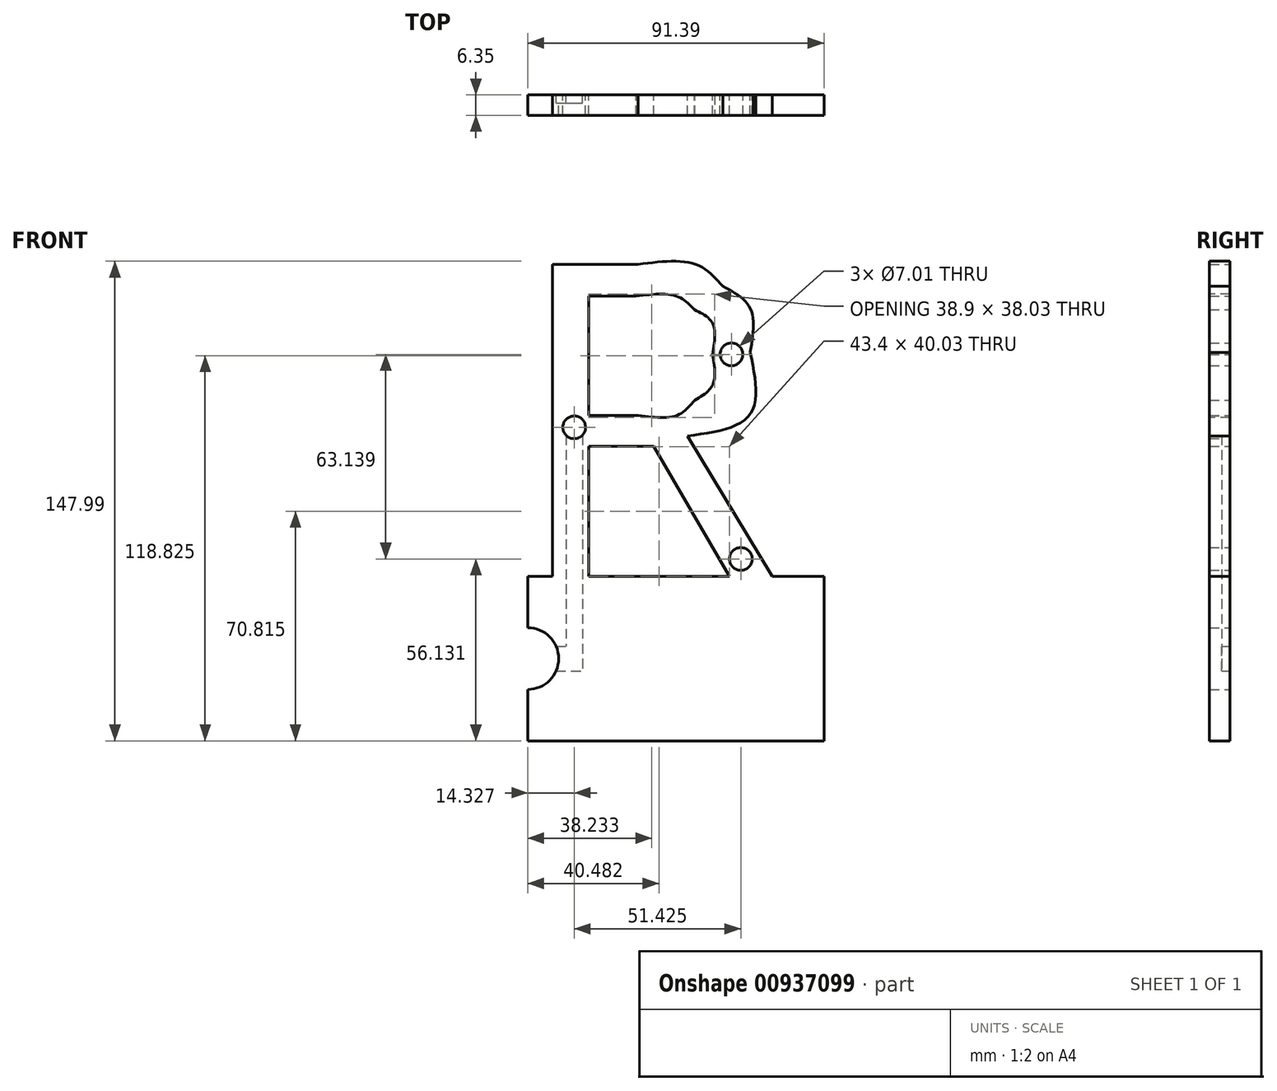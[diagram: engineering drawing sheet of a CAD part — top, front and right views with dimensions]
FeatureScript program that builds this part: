
annotation { "Feature Type Name" : "Feature", "Feature Type Description" : "" }
export const myFeature = defineFeature(function(context is Context, id is Id, definition is map)
    precondition{}
    {
        {
            var Q0;
            Q0=qCreatedBy(makeId("Front.planeOp"),FACE);
            var sketch = newSketch(context, id + "F0", { "sketchPlane" : qUnion([Q0])});
            skText(sketch, "E0", { "text": "R", "fontName": "OpenSans-Regular.ttf"});
            const initialGuessF0  = {"E0": [-0.0449, -0.04854, 1, 0, 0.09708]};
            skSetInitialGuess(sketch, initialGuessF0);
            skSolve(sketch);
        }
        {
            var Q0;
            Q0=qCreatedBy(makeId("Front.planeOp"),FACE);
            var sketch = newSketch(context, id + "F1", { "sketchPlane" : qUnion([Q0])});
            skLineSegment(sketch, "E1.0.0", {"start": v(-5.92, 37.9) * mm, "end": v(-20.48, 37.9) * mm});
            skLineSegment(sketch, "E1.0.1", {"start": v(-20.48, 37.9) * mm, "end": v(-20.48, 1.1) * mm});
            skLineSegment(sketch, "E1.0.2", {"start": v(-20.48, 1.1) * mm, "end": v(-5.12, 1.1) * mm});
            skFitSpline(sketch, "E1.0.3", {"points": [v(-5.12, 1.1) * mm, v(6.72, 1.1) * mm, v(12.25, 5.8) * mm]});
            skFitSpline(sketch, "E1.0.4", {"points": [v(12.25, 5.8) * mm, v(17.78, 10.51) * mm, v(17.78, 19.93) * mm]});
            skFitSpline(sketch, "E1.0.5", {"points": [v(17.78, 19.93) * mm, v(17.78, 29.47) * mm, v(12.16, 33.69) * mm]});
            skFitSpline(sketch, "E1.0.6", {"points": [v(12.16, 33.69) * mm, v(6.53, 37.9) * mm, v(-5.92, 37.9) * mm]});
            skLineSegment(sketch, "E2.0.0", {"start": v(-20.48, -8.51) * mm, "end": v(-0.38, -8.51) * mm});
            skLineSegment(sketch, "E2.0.1", {"start": v(-0.38, -8.51) * mm, "end": v(22.92, -48.54) * mm});
            skLineSegment(sketch, "E2.0.2", {"start": v(22.92, -48.54) * mm, "end": v(36.15, -48.54) * mm});
            skLineSegment(sketch, "E2.0.3", {"start": v(36.15, -48.54) * mm, "end": v(10, -5.29) * mm});
            skFitSpline(sketch, "E2.0.4", {"points": [v(10, -5.29) * mm, v(29.37, 1.43) * mm, v(29.37, 20.52) * mm]});
            skFitSpline(sketch, "E2.0.5", {"points": [v(29.37, 20.52) * mm, v(29.37, 34.15) * mm, v(20.9, 40.93) * mm]});
            skFitSpline(sketch, "E2.0.6", {"points": [v(20.9, 40.93) * mm, v(12.45, 47.72) * mm, v(-5.27, 47.72) * mm]});
            skLineSegment(sketch, "E2.0.7", {"start": v(-5.27, 47.72) * mm, "end": v(-31.66, 47.72) * mm});
            skLineSegment(sketch, "E2.0.8", {"start": v(-31.66, 47.72) * mm, "end": v(-31.66, -48.54) * mm});
            skLineSegment(sketch, "E2.0.9", {"start": v(-31.66, -48.54) * mm, "end": v(-20.48, -48.54) * mm});
            skLineSegment(sketch, "E2.0.10", {"start": v(-20.48, -48.54) * mm, "end": v(-20.48, -8.51) * mm});
            skLineSegment(sketch, "E3.bottom", {"start": v(-39.26, -48.54) * mm, "end": v(52.13, -48.54) * mm});
            skLineSegment(sketch, "E3.top", {"start": v(-39.26, -99.34) * mm, "end": v(52.13, -99.34) * mm});
            skLineSegment(sketch, "E3.left", {"start": v(-39.26, -48.54) * mm, "end": v(-39.26, -64.41) * mm});
            skLineSegment(sketch, "E3.right", {"start": v(52.13, -48.54) * mm, "end": v(52.13, -99.34) * mm});
            skArc(sketch, "E4", {"start": v(-39.26, -83.46) * mm, "mid": v(-29.73, -73.94) * mm, "end": v(-39.26, -64.41) * mm});
            skLineSegment(sketch, "E5.trimOffspring", {"start": v(-39.26, -83.46) * mm, "end": v(-39.26, -99.34) * mm});
            skCircle(sketch, "E6", {"center": v(26.5, -43.2) * mm, "radius": 3.5 * mm});
            skCircle(sketch, "E7", {"center": v(-24.93, -2.6) * mm, "radius": 3.5 * mm});
            skCircle(sketch, "E8", {"center": v(23.6, 19.93) * mm, "radius": 3.5 * mm});
            skSolve(sketch);
        }
        {
            var Q0;
            Q0=qSketchRegion(id+"F1",true);
            extrude(context, id + "F2", {"entities" : qUnion([Q0]), "depth" : 6.35 * mm, "offsetDistance" : 25.4 * mm});
        }
        {
            var Q0;
            Q0=makeQuery(id+"F0.imprint","IMPRINT",FACE,{"disambiguationData":[TD([[makeQuery(id+"F0.imprint","IMPRINT",EDGE,{"derivedFrom":sQuery(id+"F0.wireOp",EDGE,"E0.sketch_text.stroke-0")}),-1.0]])]});
            var sketch = newSketch(context, id + "F3", { "sketchPlane" : qUnion([Q0])});
            skCircle(sketch, "E9.0", {"center": v(-24.93, -2.6) * mm, "radius": 3.5 * mm});
            skCircle(sketch, "E10.0", {"center": v(23.6, 19.93) * mm, "radius": 3.5 * mm});
            skCircle(sketch, "E11.0", {"center": v(26.5, -43.2) * mm, "radius": 3.5 * mm});
            skLineSegment(sketch, "E12", {"start": v(-24.93, -2.6) * mm, "end": v(22.6, -2.6) * mm, "construction": true});
            skLineSegment(sketch, "E13", {"start": v(-24.93, -5.13) * mm, "end": v(-24.93, -83.84) * mm, "construction": true});
            skLineSegment(sketch, "E14.0", {"start": v(-27.47, -0.18) * mm, "end": v(-27.47, -70.13) * mm});
            skLineSegment(sketch, "E15.0", {"start": v(-22.4, -5) * mm, "end": v(-22.4, -77.75) * mm});
            skLineSegment(sketch, "E16", {"start": v(26.5, -43.2) * mm, "end": v(3.95, -5.13) * mm, "construction": true});
            skLineSegment(sketch, "E17.0", {"start": v(28.68, -41.92) * mm, "end": v(6.9, -5.13) * mm});
            skLineSegment(sketch, "E18.0", {"start": v(24.3, -44.5) * mm, "end": v(1, -5.13) * mm});
            skLineSegment(sketch, "E19.0", {"start": v(-22.52, -5.13) * mm, "end": v(1, -5.13) * mm});
            skLineSegment(sketch, "E20.0", {"start": v(-27.35, -0.05) * mm, "end": v(10.16, -0.05) * mm});
            skFitSpline(sketch, "E21", {"points": [v(23.6, 19.93) * mm, v(19.76, 6.7) * mm, v(8.86, -2.6) * mm], "startDerivative": vector(0.4, -29.86) * mm, "endDerivative": vector(-29.5, -15.37) * mm, "construction": true});
            skFitSpline(sketch, "E22.0", {"points": [v(25.19, 19.95) * mm, v(25.23, 17.3) * mm, v(24.65, 13.45) * mm, v(22.86, 8.83) * mm, v(21.07, 5.66) * mm, v(18.9, 2.83) * mm, v(16.29, 0.3) * mm, v(13.22, -1.97) * mm, v(10.86, -3.34) * mm, v(9.59, -4) * mm]});
            skFitSpline(sketch, "E23.0", {"points": [v(22.02, 19.9) * mm, v(22.05, 17.59) * mm, v(21.54, 14.23) * mm, v(19.98, 10.2) * mm, v(18.41, 7.42) * mm, v(16.52, 4.96) * mm, v(13.48, 2) * mm, v(10.5, 0.05) * mm, v(8.12, -1.18) * mm]});
            skArc(sketch, "E24.0", {"start": v(-39.26, -83.46) * mm, "mid": v(-29.73, -73.94) * mm, "end": v(-39.26, -64.41) * mm});
            skLineSegment(sketch, "E25", {"start": v(-39.26, -73.94) * mm, "end": v(-13.86, -73.94) * mm, "construction": true});
            skLineSegment(sketch, "E26.0", {"start": v(-39.26, -77.75) * mm, "end": v(-22.4, -77.75) * mm});
            skLineSegment(sketch, "E27.0", {"start": v(-39.26, -70.13) * mm, "end": v(-27.47, -70.13) * mm});
            skLineSegment(sketch, "E28", {"start": v(28.68, -41.92) * mm, "end": v(24.3, -44.5) * mm});
            skLineSegment(sketch, "E29", {"start": v(-39.26, -70.13) * mm, "end": v(-39.26, -77.75) * mm});
            skLineSegment(sketch, "E30", {"start": v(-22.4, -83.84) * mm, "end": v(-27.47, -83.84) * mm});
            skLineSegment(sketch, "E31", {"start": v(25.19, 19.95) * mm, "end": v(22.02, 19.9) * mm});
            skFitSpline(sketch, "E32", {"points": [v(15.73, -0.05) * mm, v(6.9, -5.13) * mm], "startDerivative": vector(-8.83, -5.08) * mm, "endDerivative": vector(-8.83, -5.08) * mm});
            skSolve(sketch);
        }
        {
            var Q0;
            Q0=qSketchRegion(id+"F3",true);
            extrude(context, id + "F4", {"entities" : qUnion([Q0]), "operationType" : NewBodyOperationType.REMOVE, "depth" : 2.54 * mm, "offsetDistance" : 25.4 * mm});
        }
    });
